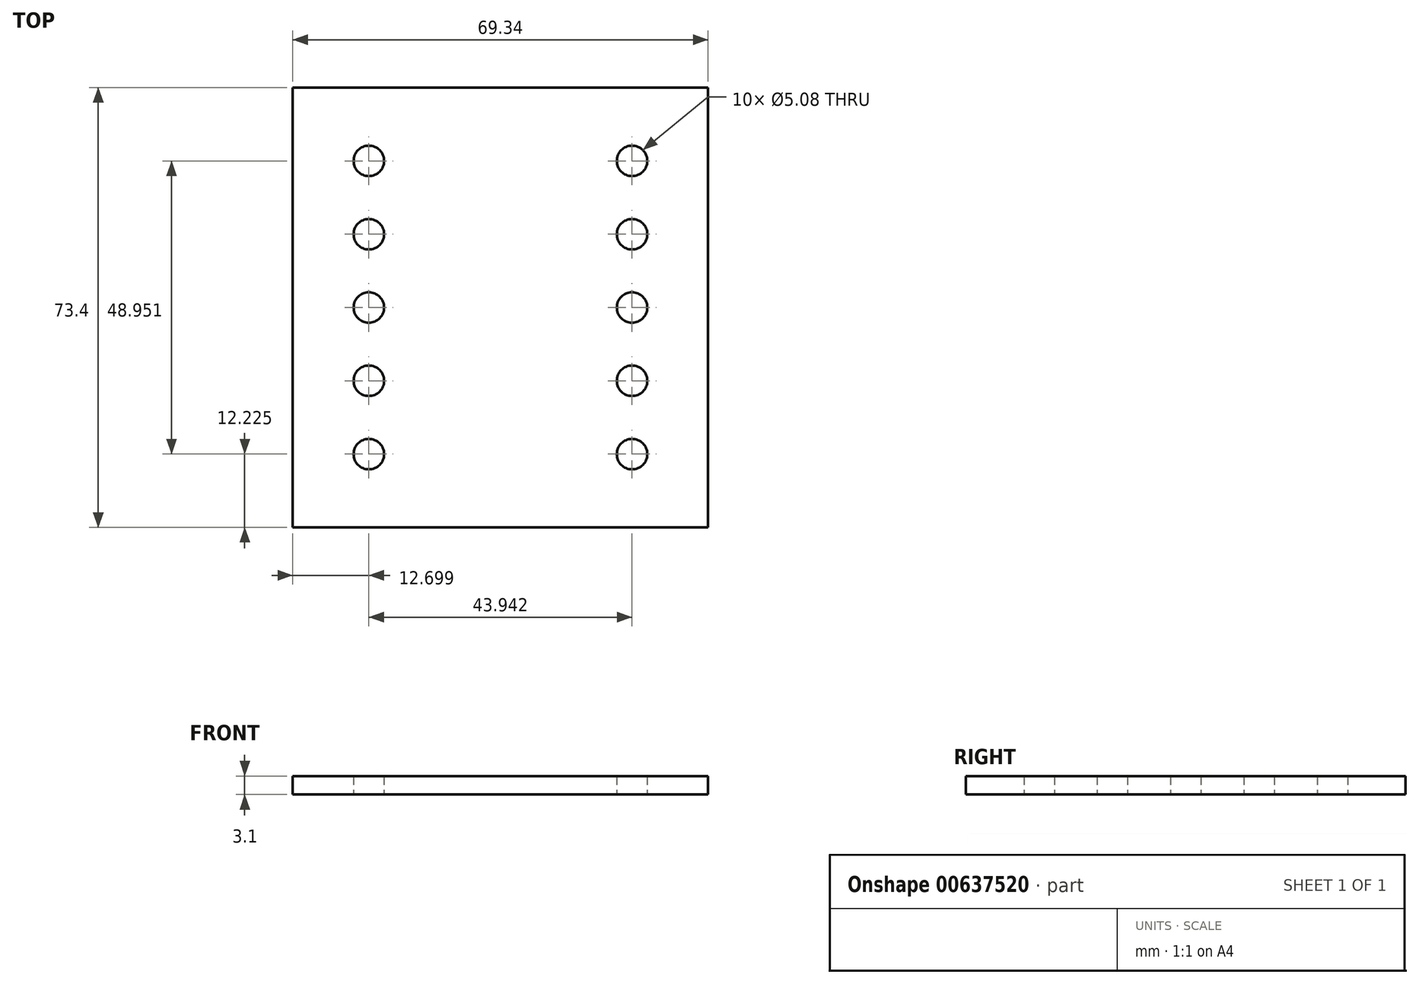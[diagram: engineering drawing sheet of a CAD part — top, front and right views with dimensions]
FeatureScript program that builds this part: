
annotation { "Feature Type Name" : "Feature", "Feature Type Description" : "" }
export const myFeature = defineFeature(function(context is Context, id is Id, definition is map)
    precondition{}
    {
        {
            var Q0;
            Q0=qCreatedBy(makeId("Top.planeOp"),FACE);
            var sketch = newSketch(context, id + "F0", { "sketchPlane" : qUnion([Q0])});
            skLineSegment(sketch, "E0.bottom", {"start": v(-34.67, 36.7) * mm, "end": v(34.67, 36.7) * mm});
            skLineSegment(sketch, "E0.top", {"start": v(-34.67, -36.7) * mm, "end": v(34.67, -36.7) * mm});
            skLineSegment(sketch, "E0.left", {"start": v(-34.67, 36.7) * mm, "end": v(-34.67, -36.7) * mm});
            skLineSegment(sketch, "E0.right", {"start": v(34.67, 36.7) * mm, "end": v(34.67, -36.7) * mm});
            skPoint(sketch, "E0.middle", {"position": v(0, 0) * mm});
            skCircle(sketch, "E1", {"center": v(-21.97, 0) * mm, "radius": 2.54 * mm});
            skCircle(sketch, "E2", {"center": v(-21.97, 12.23) * mm, "radius": 2.54 * mm});
            skCircle(sketch, "E3", {"center": v(-21.97, 24.48) * mm, "radius": 2.54 * mm});
            skCircle(sketch, "E4.MirrorC", {"center": v(-21.97, -12.23) * mm, "radius": 2.54 * mm});
            skCircle(sketch, "E5.MirrorC", {"center": v(-21.97, -24.48) * mm, "radius": 2.54 * mm});
            skCircle(sketch, "E6.MirrorC", {"center": v(21.97, 24.48) * mm, "radius": 2.54 * mm});
            skCircle(sketch, "E7.MirrorC", {"center": v(21.97, 12.23) * mm, "radius": 2.54 * mm});
            skCircle(sketch, "E8.MirrorC", {"center": v(21.97, 0) * mm, "radius": 2.54 * mm});
            skCircle(sketch, "E9.MirrorC", {"center": v(21.97, -12.23) * mm, "radius": 2.54 * mm});
            skCircle(sketch, "E10.MirrorC", {"center": v(21.97, -24.48) * mm, "radius": 2.54 * mm});
            skLineSegment(sketch, "E11.bottom", {"start": v(-21.9, 36.7) * mm, "end": v(3.18, 36.7) * mm});
            skLineSegment(sketch, "E11.top", {"start": v(-3.17, -36.7) * mm, "end": v(21.9, -36.7) * mm});
            skLineSegment(sketch, "E12.top", {"start": v(-3.18, -36.7) * mm, "end": v(21.9, -36.7) * mm});
            skLineSegment(sketch, "E13.bottom", {"start": v(-3.18, 36.7) * mm, "end": v(3.18, 36.7) * mm});
            skLineSegment(sketch, "E13.top", {"start": v(-3.24, -36.7) * mm, "end": v(21.9, -36.7) * mm});
            skLineSegment(sketch, "E14.bottom", {"start": v(3.17, 36.58) * mm, "end": v(-3.18, 36.58) * mm});
            skLineSegment(sketch, "E14.top", {"start": v(3.18, -36.58) * mm, "end": v(-3.17, -36.58) * mm});
            skSolve(sketch);
        }
        {
            var Q0;
            Q0=qSketchRegion(id+"F0",true);
            extrude(context, id + "F1", {"entities" : qUnion([Q0]), "endBound" : BoundingType.SYMMETRIC, "depth" : 3.1 * mm, "offsetDistance" : 25.4 * mm});
        }
    });
